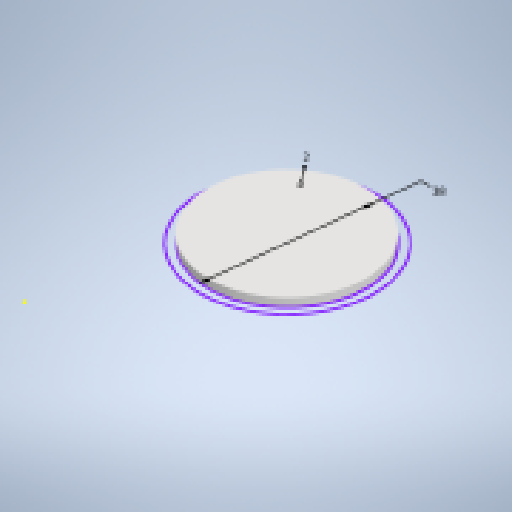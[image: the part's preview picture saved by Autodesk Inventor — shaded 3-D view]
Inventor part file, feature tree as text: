
AUTODESK INVENTOR PART (.ipt)
format: ipt  version: 2023.1 (Build 271208000, 208)  size: 807,424 bytes
history: native  units: in
note: dims shown in document units (in); Inventor stores cm internally (conversion verified against a paired STEP export)
features: extrude x5, fillet x3, other x3, plane x2, sketch x2, pattern_circular x2, chamfer x1, hole x1
ambient origin geometry x8: Origin, YZ Plane, XZ Plane, XY Plane, X Axis, Y Axis, Z Axis, Center Point
bodies: Body1 (feature_tree)
feature tree (19):
  plane  "Work Plane1"
  sketch  "Sketch1"  dims[d0=1.4961in d4=0.2559in d7=0.0787in d8=0.0in]
  extrude  "Extrusion3"  Depth=0.0787in
  chamfer  "Chamfer1"  Distance=0.0787in
  plane  "Work Plane2"
  extrude  "Extrusion5"  Depth=0.0787in TaperAngle=0.0deg
  extrude  "Extrusion6"  Depth=0.0787in
  pattern_circular  "Circular Pattern1"  [2 undecoded]
  extrude  "Extrusion7"  Depth=0.0787in TaperAngle=360.0deg
  pattern_circular  "Circular Pattern2"  [2 undecoded]
  extrude  "Extrusion8"  Depth=0.0787in TaperAngle=360.0deg
  fillet  "Fillet1"  Radius=0.3937in
  hole  "Hole1"  [1 undecoded]
  fillet  "Fillet2"  Radius=0.1969in
  fillet  "Fillet3"  Radius=0.0787in
  sketch  "Sketch2"  dims[d11=0.0787in d12=0.0787in d13=45.0deg d21=0.4537in d22=0.0in d23=0.0866in d24=0.4537in d25=0.0in d26=2.3622in d27=360.0deg d29=0.4537in d30=0.0in d31=2.3622in d32=360.0deg d34=0.3937in d35=0.0in d36=0.1181in d37=0.1772in d38=0.2362in d39=0.1575in d40=0.0787in d41=90.0deg d42=0.8312in d43=0.0in d44=0.1969in d45=0.0787in d2=0.0197in d3=0.0344in d5=0.0344in]
  other  "<userpath>\Documents\WaterPump\Assembly1.iam"
  other  "Assembly1.iam"
  other  "Motor:1"
note: 5 required parameter values undecoded (feature->parameter linkage not recoverable at this tier; creation-order binding heuristic only, values carry confidence <= 0.55)
